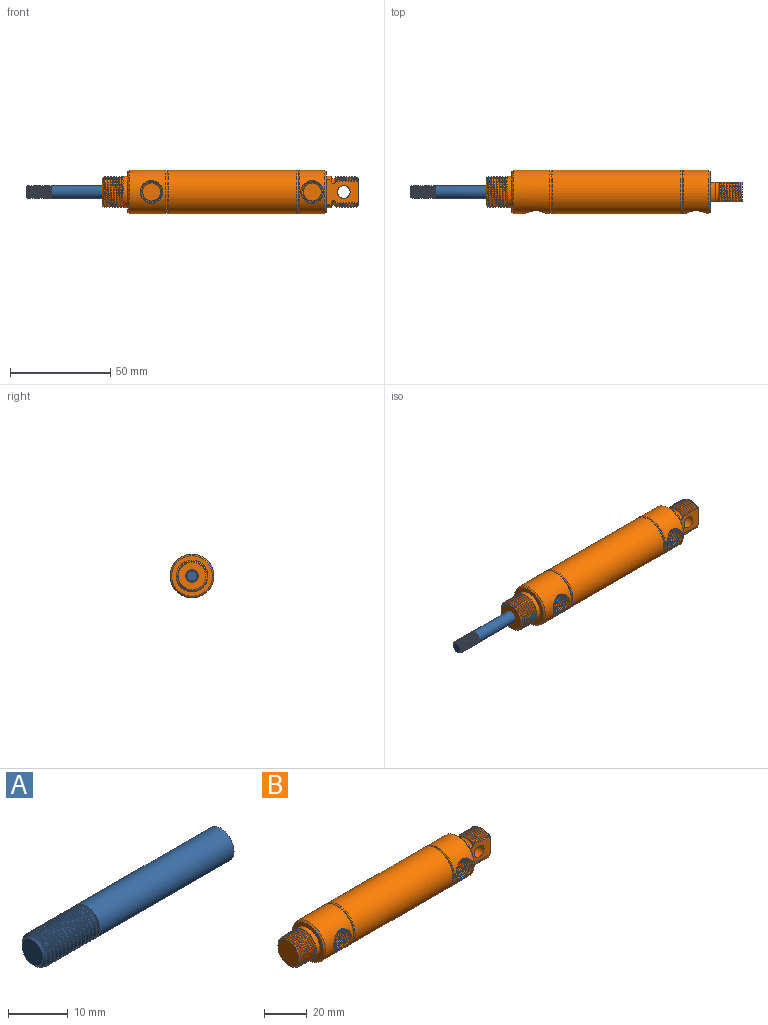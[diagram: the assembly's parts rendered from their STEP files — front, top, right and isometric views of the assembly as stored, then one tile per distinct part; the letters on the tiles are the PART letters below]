
ASSEMBLY  parts=2 mates=1
PART A: 21 faces, bbox 45.6x6.7x6.7 mm
  f0: cone r=2.49mm half-angle=45deg, axis (1,0,0), area 9.5mm2, adj f1,f15,f16,f17,f18
  f1: cylinder r=3.17mm len=6.35mm, axis (-1,0,0), area 1.3mm2, adj f0,f2,f16,f18
  f2: cylinder r=3.17mm len=6.35mm, axis (-1,0,0), area 2.3mm2, adj f1,f3,f16,f18
  f3: cylinder r=3.17mm len=6.35mm, axis (-1,0,0), area 2.3mm2, adj f2,f4,f16,f18
  f4: cylinder r=3.17mm len=6.35mm, axis (-1,0,0), area 2.3mm2, adj f3,f5,f16,f18
  f5: cylinder r=3.17mm len=6.35mm, axis (-1,0,0), area 2.3mm2, adj f4,f6,f16,f18
  f6: cylinder r=3.17mm len=6.35mm, axis (-1,0,0), area 2.3mm2, adj f5,f7,f16,f18
  f7: cylinder r=3.17mm len=6.35mm, axis (-1,0,0), area 2.3mm2, adj f6,f8,f16,f18
  f8: cylinder r=3.17mm len=6.35mm, axis (-1,0,0), area 2.3mm2, adj f7,f9,f16,f18
  f9: cylinder r=3.17mm len=6.35mm, axis (-1,0,0), area 2.3mm2, adj f8,f10,f16,f18
  f10: cylinder r=3.17mm len=6.35mm, axis (-1,0,0), area 2.3mm2, adj f9,f11,f16,f18
  f11: cylinder r=3.17mm len=6.35mm, axis (-1,0,0), area 2.3mm2, adj f10,f12,f16,f18
  f12: cylinder r=3.17mm len=6.35mm, axis (-1,0,0), area 2.3mm2, adj f11,f13,f16,f18
  f13: cylinder r=3.17mm len=6.35mm, axis (-1,0,0), area 2.3mm2, adj f12,f14,f16,f18
  f14: cylinder r=3.17mm len=32.43mm, axis (-1,0,0), area 634.9mm2, adj f13,f16,f18,f19,f20
  f15: plane 4.99x4.99mm, normal (-1,0,0), area 19.6mm2, adj f0
  f16: bspline ~13.15x6.35mm, area 167.2mm2, adj f0,f1,f2,f3,f4,f5,f6,f7
  f17: bspline ~12.84x5.1mm, area 25.6mm2, adj f0,f16,f18,f19
  f18: bspline ~13.83x6.35mm, area 181mm2, adj f0,f1,f2,f3,f4,f5,f6,f7
  f19: plane 6.7x6.7mm, normal (-1,0,0), area 5.5mm2, adj f14,f16,f17,f18
  f20: plane 6.35x6.35mm, normal (1,0,0), area 31.7mm2, adj f14
PART B: 127 faces, bbox 129.4x22.4x22.4 mm
  f0: torus R=7.56mm, axis (-1,0,0), area 33mm2, adj f49,f62,f63,f106,f108,f109
  f1: torus R=7.56mm, axis (-1,0,0), area 33.1mm2, adj f31,f32,f43,f105,f108,f109
  f2: cylinder r=5.14mm len=10.29mm, axis (0,-1,0), area 23.6mm2, adj f118,f123,f125,f126
  f3: cylinder r=5.14mm len=10.29mm, axis (0,-1,0), area 23.6mm2, adj f116,f119,f121,f122
  f4: cylinder r=5.66mm len=11.32mm, axis (0,1,0), area 14mm2, adj f24,f118
  f5: cylinder r=5.66mm len=11.32mm, axis (0,1,0), area 14mm2, adj f23,f116
  f6: cone r=7.94mm half-angle=45deg, axis (1,0,0), area 38.8mm2, adj f14,f111,f112,f113,f114
  f7: cylinder r=7.94mm len=15.88mm, axis (1,0,0), area 119mm2, adj f8,f28,f110,f111,f113
  f8: cylinder r=7.94mm len=15.88mm, axis (1,0,0), area 8.8mm2, adj f7,f9,f111,f113
  f9: cylinder r=7.94mm len=15.88mm, axis (1,0,0), area 8.8mm2, adj f8,f10,f111,f113
  f10: cylinder r=7.94mm len=15.88mm, axis (1,0,0), area 8.8mm2, adj f9,f11,f111,f113
  f11: cylinder r=7.94mm len=15.88mm, axis (1,0,0), area 8.8mm2, adj f10,f12,f111,f113
  f12: cylinder r=7.94mm len=15.88mm, axis (1,0,0), area 8.8mm2, adj f11,f13,f111,f113
  f13: cylinder r=7.94mm len=15.88mm, axis (1,0,0), area 8.8mm2, adj f12,f14,f111,f113
  f14: cylinder r=7.94mm len=5.61mm, axis (1,0,0), area 0.5mm2, adj f6,f13,f113
  f15: cylinder r=3.17mm len=9.65mm, axis (0,-1,0), area 192.5mm2, adj f108,f109
  f16: cone r=10.92mm half-angle=45deg, axis (-1,0,0), area 71.4mm2, adj f24,f27
  f17: cone r=10.38mm half-angle=45deg, axis (1,0,0), area 51.7mm2, adj f24,f30
  f18: cone r=10.92mm half-angle=26.6deg, axis (-1,0,0), area 41.4mm2, adj f22,f30
  f19: cone r=10.65mm half-angle=26.6deg, axis (1,0,0), area 41.4mm2, adj f22,f29
  f20: cone r=10.92mm half-angle=45deg, axis (-1,0,0), area 51.7mm2, adj f23,f29
  f21: cone r=10.16mm half-angle=45deg, axis (1,0,0), area 71.4mm2, adj f23,f28
  f22: cylinder r=10.92mm len=64.33mm, axis (-1,0,0), area 4414.8mm2, adj f18,f19
  f23: cylinder r=10.92mm len=21.84mm, axis (-1,0,0), area 1174.2mm2, adj f5,f20,f21,f115
  f24: cylinder r=10.92mm len=21.84mm, axis (-1,0,0), area 800.7mm2, adj f4,f16,f17,f117
  f25: cone r=5.14mm half-angle=45deg, axis (0,-1,0), area 13.3mm2, adj f116,f119,f120,f121
  f26: cone r=5.14mm half-angle=45deg, axis (0,-1,0), area 13.3mm2, adj f118,f123,f124,f125
  f27: plane 20.32x20.32mm, normal (1,0,0), area 181.1mm2, adj f16,f47,f107,f108,f109
  f28: plane 20.32x20.32mm, normal (-1,0,0), area 126.4mm2, adj f7,f21
  f29: plane 21.3x21.3mm, normal (-1,0,0), area 18mm2, adj f19,f20
  f30: plane 21.3x21.3mm, normal (1,0,0), area 18mm2, adj f17,f18
  f31: bspline ~5.61x2.97mm, area 0mm2, adj f1,f32,f109
  f32: bspline ~5.48x1.92mm, area 0.6mm2, adj f1,f31,f43,f109
  f33: cylinder r=7.94mm len=9.65mm, axis (1,0,0), area 1.8mm2, adj f39,f41,f108,f109
  f34: bspline ~9.93x2.06mm, area 1.9mm2, adj f37,f40,f108,f109
  f35: bspline ~9.93x2.06mm, area 1.9mm2, adj f38,f41,f108,f109
  f36: bspline ~9.65x1.92mm, area 1.9mm2, adj f39,f81,f108,f109
  f37: bspline ~11.23x2.97mm, area 9.8mm2, adj f34,f77,f108,f109
  f38: bspline ~10.91x2.84mm, area 11.2mm2, adj f35,f44,f108,f109
  f39: bspline ~10.91x2.84mm, area 11.2mm2, adj f33,f36,f108,f109
  f40: bspline ~11.23x2.97mm, area 11.2mm2, adj f34,f44,f108,f109
  f41: bspline ~11.23x2.97mm, area 11.2mm2, adj f33,f35,f108,f109
  f42: cylinder r=7.94mm len=9.65mm, axis (1,0,0), area 1.8mm2, adj f43,f66,f108,f109
  f43: bspline ~11.23x2.97mm, area 9.9mm2, adj f1,f32,f42,f108,f109
  f44: cylinder r=7.94mm len=9.65mm, axis (1,0,0), area 1.8mm2, adj f38,f40,f108,f109
  f45: cone r=6.88mm half-angle=45deg, axis (-1,0,0), area 7.5mm2, adj f56,f78,f108,f109
  f46: plane 9.71x2.78mm, normal (1,0,0), area 9.2mm2, adj f62,f63,f64,f107,f108,f109
  f47: cylinder r=7.94mm len=9.65mm, axis (1,0,0), area 23.7mm2, adj f27,f105,f108,f109
  f48: cylinder r=7.94mm len=1.02mm, axis (1,0,0), area 0mm2, adj f49,f106,f108
  f49: bspline ~11.23x2.97mm, area 8.7mm2, adj f0,f48,f50,f106,f108,f109
  f50: bspline ~9.65x1.92mm, area 1.9mm2, adj f49,f67,f108,f109
  f51: cylinder r=7.94mm len=9.65mm, axis (1,0,0), area 1.8mm2, adj f61,f84,f108,f109
  f52: cylinder r=7.94mm len=9.65mm, axis (1,0,0), area 1.8mm2, adj f58,f60,f108,f109
  f53: bspline ~9.93x2.06mm, area 1.9mm2, adj f56,f59,f108,f109
  f54: bspline ~9.65x1.92mm, area 1.9mm2, adj f57,f60,f108,f109
  f55: bspline ~9.65x1.92mm, area 1.9mm2, adj f58,f61,f108,f109
  f56: bspline ~11.23x2.97mm, area 4.4mm2, adj f45,f53,f108,f109
  f57: bspline ~11.23x2.97mm, area 11.2mm2, adj f54,f76,f108,f109
  f58: bspline ~11.23x2.97mm, area 11.2mm2, adj f52,f55,f108,f109
  f59: bspline ~11.23x2.97mm, area 11.2mm2, adj f53,f76,f108,f109
  f60: bspline ~11.23x2.97mm, area 11.2mm2, adj f52,f54,f108,f109
  f61: bspline ~10.91x2.84mm, area 11.2mm2, adj f51,f55,f108,f109
  f62: bspline ~6.59x1.92mm, area 0.6mm2, adj f0,f46,f63,f64,f108
  f63: bspline ~11.23x2.97mm, area 0.7mm2, adj f0,f46,f62,f109
  f64: bspline ~1.33x1.03mm, area 0.1mm2, adj f46,f62,f108
  f65: cylinder r=7.94mm len=9.65mm, axis (1,0,0), area 1.8mm2, adj f67,f103,f108,f109
  f66: bspline ~10.91x2.84mm, area 11.2mm2, adj f42,f68,f108,f109
  f67: bspline ~10.91x2.84mm, area 11.2mm2, adj f50,f65,f108,f109
  f68: bspline ~9.65x1.92mm, area 1.9mm2, adj f66,f104,f108,f109
  f69: cylinder r=7.94mm len=9.65mm, axis (1,0,0), area 1.8mm2, adj f81,f87,f108,f109
  f70: cylinder r=7.94mm len=9.65mm, axis (1,0,0), area 1.8mm2, adj f85,f90,f108,f109
  f71: cylinder r=7.94mm len=9.65mm, axis (1,0,0), area 1.8mm2, adj f88,f93,f108,f109
  f72: cylinder r=7.94mm len=9.65mm, axis (1,0,0), area 1.8mm2, adj f91,f96,f108,f109
  f73: cylinder r=7.94mm len=9.65mm, axis (1,0,0), area 1.8mm2, adj f94,f99,f108,f109
  f74: cylinder r=7.94mm len=9.65mm, axis (1,0,0), area 1.8mm2, adj f97,f102,f108,f109
  f75: cylinder r=7.94mm len=9.65mm, axis (1,0,0), area 1.8mm2, adj f100,f104,f108,f109
  f76: cylinder r=7.94mm len=9.65mm, axis (1,0,0), area 1.8mm2, adj f57,f59,f108,f109
  f77: cone r=6.88mm half-angle=45deg, axis (-1,0,0), area 12mm2, adj f37,f78,f79,f80,f82,f108,f109
  f78: plane 13.76x9.65mm, normal (1,0,0), area 120.9mm2, adj f45,f77,f108,f109
  f79: bspline ~9.93x2.06mm, area 0.7mm2, adj f77,f80,f82,f108
  f80: bspline ~5.61x2.97mm, area 0mm2, adj f77,f79,f108
  f81: bspline ~11.23x2.97mm, area 11.2mm2, adj f36,f69,f108,f109
  f82: bspline ~11.23x2.97mm, area 1.7mm2, adj f77,f79,f108
  f83: bspline ~9.93x2.06mm, area 1.9mm2, adj f84,f85,f108,f109
  f84: bspline ~11.23x2.97mm, area 11.2mm2, adj f51,f83,f108,f109
  f85: bspline ~10.91x2.84mm, area 11.2mm2, adj f70,f83,f108,f109
  f86: bspline ~9.65x1.92mm, area 1.9mm2, adj f87,f88,f108,f109
  f87: bspline ~11.23x2.97mm, area 11.2mm2, adj f69,f86,f108,f109
  f88: bspline ~11.23x2.97mm, area 11.2mm2, adj f71,f86,f108,f109
  f89: bspline ~9.93x2.06mm, area 1.9mm2, adj f90,f91,f108,f109
  f90: bspline ~11.23x2.97mm, area 11.2mm2, adj f70,f89,f108,f109
  f91: bspline ~11.23x2.97mm, area 11.2mm2, adj f72,f89,f108,f109
  f92: bspline ~9.93x2.06mm, area 1.9mm2, adj f93,f94,f108,f109
  f93: bspline ~11.23x2.97mm, area 11.2mm2, adj f71,f92,f108,f109
  f94: bspline ~11.23x2.97mm, area 11.2mm2, adj f73,f92,f108,f109
  f95: bspline ~9.93x2.06mm, area 1.9mm2, adj f96,f97,f108,f109
  f96: bspline ~11.23x2.97mm, area 11.2mm2, adj f72,f95,f108,f109
  f97: bspline ~11.23x2.97mm, area 11.2mm2, adj f74,f95,f108,f109
  f98: bspline ~9.65x1.92mm, area 1.9mm2, adj f99,f100,f108,f109
  f99: bspline ~11.23x2.97mm, area 11.2mm2, adj f73,f98,f108,f109
  f100: bspline ~11.23x2.97mm, area 11.2mm2, adj f75,f98,f108,f109
  f101: bspline ~9.93x2.06mm, area 1.9mm2, adj f102,f103,f108,f109
  f102: bspline ~10.91x2.84mm, area 11.2mm2, adj f74,f101,f108,f109
  f103: bspline ~11.23x2.97mm, area 11.2mm2, adj f65,f101,f108,f109
  f104: bspline ~11.23x2.97mm, area 11.2mm2, adj f68,f75,f108,f109
  f105: plane 9.65x2.12mm, normal (1,0,0), area 4mm2, adj f1,f47,f108,f109
  f106: plane 8.39x2.07mm, normal (-1,0,0), area 1.9mm2, adj f0,f48,f49,f108
  f107: cylinder r=7.94mm len=9.65mm, axis (1,0,0), area 23.7mm2, adj f27,f46,f108,f109
  f108: plane 16.05x12.91mm, normal (0,-1,0), area 145.2mm2, adj f0,f1,f15,f27,f33,f34,f35,f36
  f109: plane 16.05x12.91mm, normal (0,1,0), area 144.8mm2, adj f0,f1,f15,f27,f31,f32,f33,f34
  f110: plane 16.44x16.44mm, normal (-1,0,0), area 21.9mm2, adj f7,f111,f112,f113
  f111: bspline ~15.86x15.85mm, area 345.7mm2, adj f6,f7,f8,f9,f10,f11,f12,f13
  f112: bspline ~14.03x14.03mm, area 56.6mm2, adj f6,f110,f111,f113
  f113: bspline ~15.88x15.88mm, area 345.1mm2, adj f6,f7,f8,f9,f10,f11,f12,f13
  f114: plane 13.76x13.76mm, normal (-1,0,0), area 148.7mm2, adj f6
  f115: cylinder r=5.66mm len=11.32mm, axis (0,1,0), area 0mm2, adj f23,f116
  f116: plane 11.32x11.32mm, normal (0,-1,0), area 17.5mm2, adj f3,f5,f25,f115
  f117: cylinder r=5.66mm len=11.32mm, axis (0,1,0), area 0mm2, adj f24,f118
  f118: plane 11.32x11.32mm, normal (0,-1,0), area 17.5mm2, adj f2,f4,f26,f117
  f119: bspline ~10.29x10.29mm, area 115.6mm2, adj f3,f25,f120,f122
  f120: bspline ~9.06x9.05mm, area 18.6mm2, adj f25,f119,f121,f122
  f121: bspline ~10.28x10.27mm, area 126.4mm2, adj f3,f25,f120,f122
  f122: plane 10.11x10.1mm, normal (0,-1,0), area 73.7mm2, adj f3,f119,f120,f121
  f123: bspline ~10.29x10.29mm, area 115.6mm2, adj f2,f26,f124,f126
  f124: bspline ~9.06x9.05mm, area 18.6mm2, adj f26,f123,f125,f126
  f125: bspline ~10.28x10.27mm, area 126.4mm2, adj f2,f26,f124,f126
  f126: plane 10.11x10.1mm, normal (0,-1,0), area 73.7mm2, adj f2,f123,f124,f125
PLACE A t=(-32.14,-0.2,0.04)mm
PLACE B t=(-6.74,-0.2,0.04)mm fixed
MATE slider A.f0 <-> B.f6  axis (1,0,0) through (-57.92,-0.2,0.04)mm
